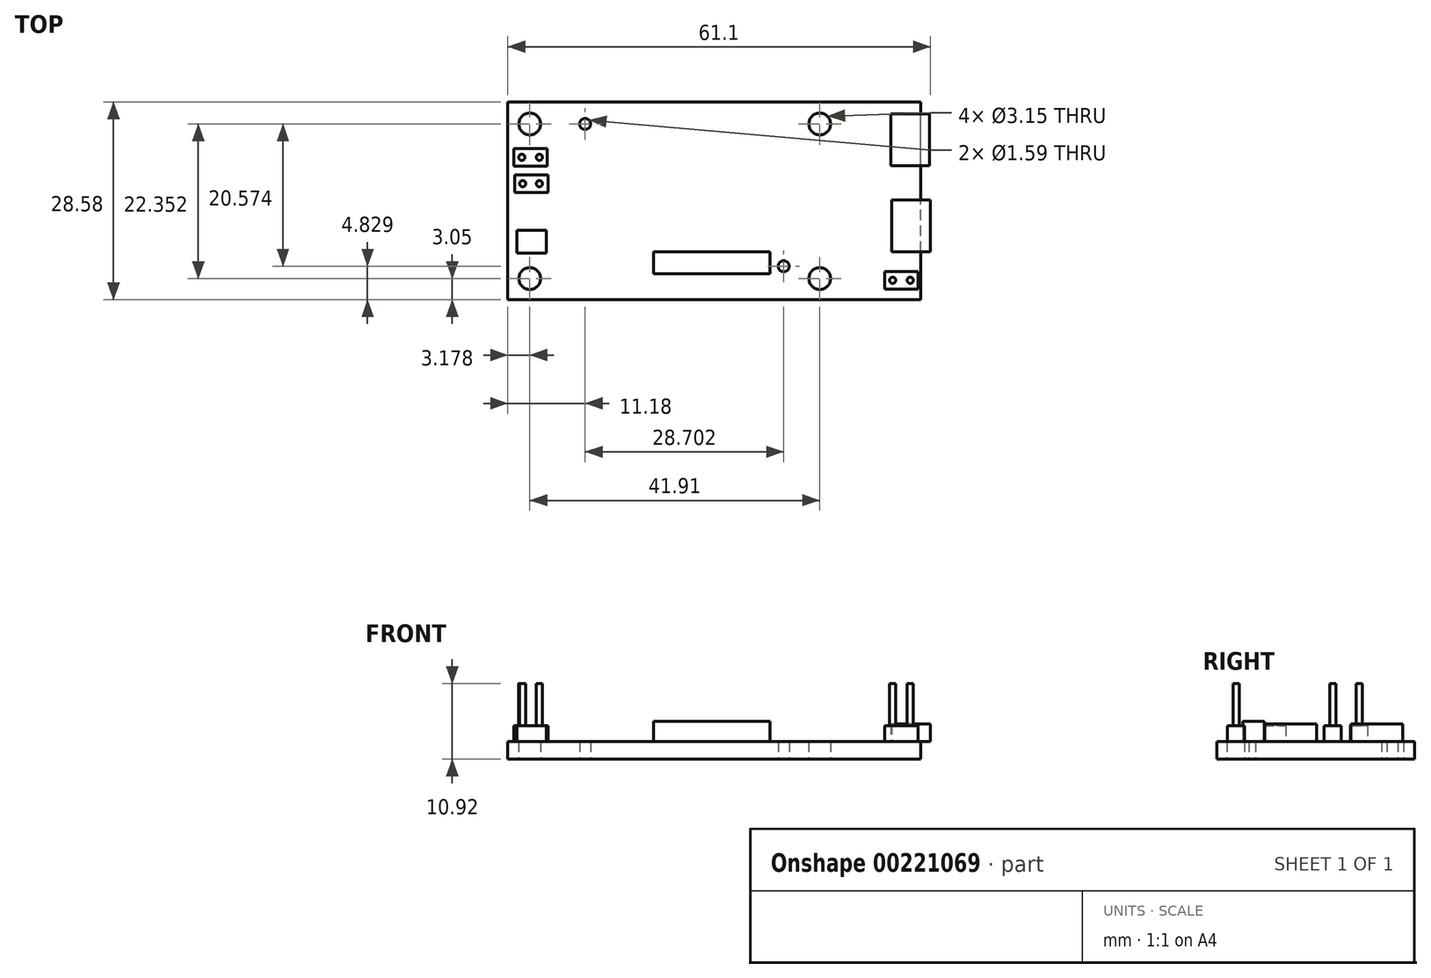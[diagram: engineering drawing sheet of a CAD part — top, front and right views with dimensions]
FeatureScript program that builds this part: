
annotation { "Feature Type Name" : "Feature", "Feature Type Description" : "" }
export const myFeature = defineFeature(function(context is Context, id is Id, definition is map)
    precondition{}
    {
        {
            var Q0;
            Q0=qCreatedBy(makeId("Top.planeOp"),FACE);
            var sketch = newSketch(context, id + "F0", { "sketchPlane" : qUnion([Q0])});
            skLineSegment(sketch, "E0", {"start": v(-22.44, -2) * mm, "end": v(-22.44, -0.67) * mm});
            skLineSegment(sketch, "E1", {"start": v(-22.44, -0.67) * mm, "end": v(-21.12, -0.67) * mm});
            skLineSegment(sketch, "E2", {"start": v(-21.12, -0.67) * mm, "end": v(-21.12, -2) * mm});
            skLineSegment(sketch, "E3", {"start": v(-21.12, -2) * mm, "end": v(-22.44, -2) * mm});
            skLineSegment(sketch, "E4", {"start": v(-22.44, 0.55) * mm, "end": v(-22.44, 1.87) * mm});
            skLineSegment(sketch, "E5", {"start": v(-22.44, 1.87) * mm, "end": v(-21.12, 1.87) * mm});
            skLineSegment(sketch, "E6", {"start": v(-21.12, 1.87) * mm, "end": v(-21.12, 0.55) * mm});
            skLineSegment(sketch, "E7", {"start": v(-21.12, 0.55) * mm, "end": v(-22.44, 0.55) * mm});
            skLineSegment(sketch, "E8", {"start": v(-22.44, 3.09) * mm, "end": v(-22.44, 4.4) * mm});
            skLineSegment(sketch, "E9", {"start": v(-22.44, 4.4) * mm, "end": v(-21.12, 4.4) * mm});
            skLineSegment(sketch, "E10", {"start": v(-21.12, 4.4) * mm, "end": v(-21.12, 3.09) * mm});
            skLineSegment(sketch, "E11", {"start": v(-21.12, 3.09) * mm, "end": v(-22.44, 3.09) * mm});
            skLineSegment(sketch, "E12", {"start": v(-22.44, 5.63) * mm, "end": v(-22.44, 6.95) * mm});
            skLineSegment(sketch, "E13", {"start": v(-22.44, 6.95) * mm, "end": v(-21.12, 6.95) * mm});
            skLineSegment(sketch, "E14", {"start": v(-21.12, 6.95) * mm, "end": v(-21.12, 5.63) * mm});
            skLineSegment(sketch, "E15", {"start": v(-21.12, 5.63) * mm, "end": v(-22.44, 5.63) * mm});
            skLineSegment(sketch, "E16", {"start": v(26.9, -10.78) * mm, "end": v(28.33, -10.78) * mm});
            skLineSegment(sketch, "E17", {"start": v(28.33, -10.78) * mm, "end": v(28.33, -12.2) * mm});
            skLineSegment(sketch, "E18", {"start": v(28.33, -12.2) * mm, "end": v(26.9, -12.2) * mm});
            skLineSegment(sketch, "E19", {"start": v(26.9, -12.2) * mm, "end": v(26.9, -10.78) * mm});
            skLineSegment(sketch, "E20", {"start": v(-27.68, 1.77) * mm, "end": v(-29.1, 1.77) * mm});
            skLineSegment(sketch, "E21", {"start": v(-29.1, 1.77) * mm, "end": v(-29.1, 3.19) * mm});
            skLineSegment(sketch, "E22", {"start": v(-29.1, 3.19) * mm, "end": v(-27.68, 3.19) * mm});
            skLineSegment(sketch, "E23", {"start": v(-27.68, 3.19) * mm, "end": v(-27.68, 1.77) * mm});
            skLineSegment(sketch, "E24", {"start": v(-27.8, 5.58) * mm, "end": v(-29.23, 5.58) * mm});
            skLineSegment(sketch, "E25", {"start": v(-29.23, 5.58) * mm, "end": v(-29.23, 7) * mm});
            skLineSegment(sketch, "E26", {"start": v(-29.23, 7) * mm, "end": v(-27.8, 7) * mm});
            skLineSegment(sketch, "E27", {"start": v(-27.8, 7) * mm, "end": v(-27.8, 5.58) * mm});
            skLineSegment(sketch, "E28", {"start": v(24.95, -7.37) * mm, "end": v(30.55, -7.37) * mm});
            skLineSegment(sketch, "E29", {"start": v(30.55, -7.37) * mm, "end": v(30.55, 0.13) * mm});
            skLineSegment(sketch, "E30", {"start": v(30.55, 0.13) * mm, "end": v(24.95, 0.13) * mm});
            skLineSegment(sketch, "E31", {"start": v(24.95, 0.13) * mm, "end": v(24.95, -7.37) * mm});
            skLineSegment(sketch, "E32", {"start": v(-29.24, -4.28) * mm, "end": v(-25, -4.28) * mm});
            skLineSegment(sketch, "E33", {"start": v(-25, -4.28) * mm, "end": v(-25, -7.53) * mm});
            skLineSegment(sketch, "E34", {"start": v(-25, -7.53) * mm, "end": v(-29.24, -7.53) * mm});
            skLineSegment(sketch, "E35", {"start": v(-29.24, -7.53) * mm, "end": v(-29.24, -4.28) * mm});
            skLineSegment(sketch, "E36", {"start": v(-23.05, -0.06) * mm, "end": v(-23.05, -2.6) * mm});
            skLineSegment(sketch, "E37", {"start": v(-23.05, -2.6) * mm, "end": v(2.35, -2.6) * mm});
            skLineSegment(sketch, "E38", {"start": v(2.35, -0.06) * mm, "end": v(-23.05, -0.06) * mm});
            skLineSegment(sketch, "E39", {"start": v(-23.05, 2.48) * mm, "end": v(-23.05, -0.06) * mm});
            skLineSegment(sketch, "E40", {"start": v(-23.05, -0.06) * mm, "end": v(2.35, -0.06) * mm});
            skLineSegment(sketch, "E41", {"start": v(2.35, 2.48) * mm, "end": v(-23.05, 2.48) * mm});
            skLineSegment(sketch, "E42", {"start": v(-23.05, 5.02) * mm, "end": v(-23.05, 2.48) * mm});
            skLineSegment(sketch, "E43", {"start": v(-23.05, 2.48) * mm, "end": v(2.35, 2.48) * mm});
            skLineSegment(sketch, "E44", {"start": v(2.35, 5.02) * mm, "end": v(-23.05, 5.02) * mm});
            skLineSegment(sketch, "E45", {"start": v(-23.05, 7.56) * mm, "end": v(-23.05, 5.02) * mm});
            skLineSegment(sketch, "E46", {"start": v(-23.05, 5.02) * mm, "end": v(2.35, 5.02) * mm});
            skLineSegment(sketch, "E47", {"start": v(2.35, 7.56) * mm, "end": v(-23.05, 7.56) * mm});
            skLineSegment(sketch, "E48", {"start": v(-9.46, -7.4) * mm, "end": v(7.34, -7.4) * mm});
            skLineSegment(sketch, "E49", {"start": v(7.34, -7.4) * mm, "end": v(7.34, -10.53) * mm});
            skLineSegment(sketch, "E50", {"start": v(7.34, -10.53) * mm, "end": v(-9.46, -10.53) * mm});
            skLineSegment(sketch, "E51", {"start": v(-9.46, -10.53) * mm, "end": v(-9.46, -7.4) * mm});
            skLineSegment(sketch, "E52", {"start": v(24.82, 5.08) * mm, "end": v(30.42, 5.08) * mm});
            skLineSegment(sketch, "E53", {"start": v(30.42, 5.08) * mm, "end": v(30.42, 12.58) * mm});
            skLineSegment(sketch, "E54", {"start": v(30.42, 12.58) * mm, "end": v(24.82, 12.58) * mm});
            skLineSegment(sketch, "E55", {"start": v(24.82, 12.58) * mm, "end": v(24.82, 5.08) * mm});
            skLineSegment(sketch, "E56", {"start": v(28.76, -10.25) * mm, "end": v(28.76, -12.74) * mm});
            skLineSegment(sketch, "E57", {"start": v(28.76, -12.74) * mm, "end": v(23.94, -12.74) * mm});
            skLineSegment(sketch, "E58", {"start": v(23.94, -12.74) * mm, "end": v(23.94, -10.25) * mm});
            skLineSegment(sketch, "E59", {"start": v(23.94, -10.25) * mm, "end": v(28.76, -10.25) * mm});
            skLineSegment(sketch, "E60", {"start": v(-29.53, 1.23) * mm, "end": v(-29.53, 3.72) * mm});
            skLineSegment(sketch, "E61", {"start": v(-29.53, 3.72) * mm, "end": v(-24.7, 3.72) * mm});
            skLineSegment(sketch, "E62", {"start": v(-24.7, 3.72) * mm, "end": v(-24.7, 1.23) * mm});
            skLineSegment(sketch, "E63", {"start": v(-24.7, 1.23) * mm, "end": v(-29.53, 1.23) * mm});
            skLineSegment(sketch, "E64", {"start": v(-29.66, 5.04) * mm, "end": v(-29.66, 7.53) * mm});
            skLineSegment(sketch, "E65", {"start": v(-29.66, 7.53) * mm, "end": v(-24.83, 7.53) * mm});
            skLineSegment(sketch, "E66", {"start": v(-24.83, 7.53) * mm, "end": v(-24.83, 5.04) * mm});
            skLineSegment(sketch, "E67", {"start": v(-24.83, 5.04) * mm, "end": v(-29.66, 5.04) * mm});
            skLineSegment(sketch, "E68", {"start": v(12.25, 5.02) * mm, "end": v(-13.15, 5.02) * mm});
            skLineSegment(sketch, "E69", {"start": v(-13.15, 5.02) * mm, "end": v(12.25, 5.02) * mm});
            skLineSegment(sketch, "E70", {"start": v(12.25, 5.02) * mm, "end": v(12.25, 7.56) * mm});
            skLineSegment(sketch, "E71", {"start": v(12.25, 7.56) * mm, "end": v(-13.15, 7.56) * mm});
            skLineSegment(sketch, "E72", {"start": v(12.25, -0.06) * mm, "end": v(-13.15, -0.06) * mm});
            skLineSegment(sketch, "E73", {"start": v(-13.15, -0.06) * mm, "end": v(12.25, -0.06) * mm});
            skLineSegment(sketch, "E74", {"start": v(12.25, -0.06) * mm, "end": v(12.25, 2.48) * mm});
            skLineSegment(sketch, "E75", {"start": v(12.25, 2.48) * mm, "end": v(-13.15, 2.48) * mm});
            skLineSegment(sketch, "E76", {"start": v(-13.15, 2.48) * mm, "end": v(12.25, 2.48) * mm});
            skLineSegment(sketch, "E77", {"start": v(12.25, 2.48) * mm, "end": v(12.25, 5.02) * mm});
            skLineSegment(sketch, "E78", {"start": v(-13.15, -2.6) * mm, "end": v(12.25, -2.6) * mm});
            skLineSegment(sketch, "E79", {"start": v(12.25, -2.6) * mm, "end": v(12.25, -0.06) * mm});
            skLineSegment(sketch, "E80", {"start": v(-30.55, 14.29) * mm, "end": v(-30.55, -14.29) * mm});
            skLineSegment(sketch, "E81", {"start": v(-30.55, -14.29) * mm, "end": v(29.14, -14.29) * mm});
            skLineSegment(sketch, "E82", {"start": v(29.14, -14.29) * mm, "end": v(29.14, 14.29) * mm});
            skLineSegment(sketch, "E83", {"start": v(29.14, 14.29) * mm, "end": v(-30.55, 14.29) * mm});
            skSolve(sketch);
        }
        {
            var Q0;
            Q0=qCreatedBy(makeId("Top.planeOp"),FACE);
            var sketch = newSketch(context, id + "F1", { "sketchPlane" : qUnion([Q0])});
            skLineSegment(sketch, "E84.0", {"start": v(-30.55, 14.29) * mm, "end": v(-30.55, -14.29) * mm});
            skLineSegment(sketch, "E84.1", {"start": v(-30.55, -14.29) * mm, "end": v(29.14, -14.29) * mm});
            skLineSegment(sketch, "E84.2", {"start": v(29.14, 14.29) * mm, "end": v(-30.55, 14.29) * mm});
            skLineSegment(sketch, "E84.3", {"start": v(29.14, -14.29) * mm, "end": v(29.14, 14.29) * mm});
            skCircle(sketch, "E85", {"center": v(-27.37, 11.11) * mm, "radius": 1.57 * mm});
            skCircle(sketch, "E86", {"center": v(14.54, 11.11) * mm, "radius": 1.57 * mm});
            skCircle(sketch, "E87", {"center": v(14.54, -11.24) * mm, "radius": 1.57 * mm});
            skCircle(sketch, "E88", {"center": v(-27.37, -11.24) * mm, "radius": 1.57 * mm});
            skCircle(sketch, "E89", {"center": v(-19.37, 11.11) * mm, "radius": 0.8 * mm});
            skCircle(sketch, "E90", {"center": v(9.33, -9.46) * mm, "radius": 0.8 * mm});
            skSolve(sketch);
        }
        {
            var Q0;
            Q0=qSketchRegion(id+"F1",true);
            extrude(context, id + "F2", {"entities" : qUnion([Q0]), "depth" : 2.54 * mm});
        }
        {
            var Q0;
            Q0=makeQuery(id+"F2.opExtrude","CAP_FACE",FACE,{"disambiguationData":[OSD([sQuery(id+"F1.wireOp",EDGE,"E84.0"),sQuery(id+"F1.wireOp",EDGE,"E84.1"),sQuery(id+"F1.wireOp",EDGE,"E84.2"),sQuery(id+"F1.wireOp",EDGE,"E84.3"),sQuery(id+"F1.wireOp",EDGE,"E85"),sQuery(id+"F1.wireOp",EDGE,"E86"),sQuery(id+"F1.wireOp",EDGE,"E87"),sQuery(id+"F1.wireOp",EDGE,"E88"),sQuery(id+"F1.wireOp",EDGE,"E89"),sQuery(id+"F1.wireOp",EDGE,"E90")])],"isStart":false});
            var sketch = newSketch(context, id + "F3", { "sketchPlane" : qUnion([Q0])});
            skLineSegment(sketch, "E91.0", {"start": v(30.42, 12.58) * mm, "end": v(24.82, 12.58) * mm});
            skLineSegment(sketch, "E91.1", {"start": v(30.42, 5.08) * mm, "end": v(30.42, 12.58) * mm});
            skLineSegment(sketch, "E91.2", {"start": v(24.82, 5.08) * mm, "end": v(30.42, 5.08) * mm});
            skLineSegment(sketch, "E91.3", {"start": v(24.82, 12.58) * mm, "end": v(24.82, 5.08) * mm});
            skLineSegment(sketch, "E91.4", {"start": v(30.55, 0.13) * mm, "end": v(24.95, 0.13) * mm});
            skLineSegment(sketch, "E91.5", {"start": v(30.55, -7.37) * mm, "end": v(30.55, 0.13) * mm});
            skLineSegment(sketch, "E91.6", {"start": v(24.95, -7.37) * mm, "end": v(30.55, -7.37) * mm});
            skLineSegment(sketch, "E91.7", {"start": v(24.95, 0.13) * mm, "end": v(24.95, -7.37) * mm});
            skSolve(sketch);
        }
        {
            var Q0;
            Q0=qSketchRegion(id+"F3",true);
            extrude(context, id + "F4", {"entities" : qUnion([Q0]), "operationType" : NewBodyOperationType.ADD, "depth" : 2.54 * mm});
        }
        {
            var Q0;
            Q0=makeQuery(id+"F2.opExtrude","CAP_FACE",FACE,{"disambiguationData":[OSD([sQuery(id+"F1.wireOp",EDGE,"E84.0"),sQuery(id+"F1.wireOp",EDGE,"E84.1"),sQuery(id+"F1.wireOp",EDGE,"E84.2"),sQuery(id+"F1.wireOp",EDGE,"E84.3"),sQuery(id+"F1.wireOp",EDGE,"E85"),sQuery(id+"F1.wireOp",EDGE,"E86"),sQuery(id+"F1.wireOp",EDGE,"E87"),sQuery(id+"F1.wireOp",EDGE,"E88"),sQuery(id+"F1.wireOp",EDGE,"E89"),sQuery(id+"F1.wireOp",EDGE,"E90")])],"isStart":false});
            var sketch = newSketch(context, id + "F5", { "sketchPlane" : qUnion([Q0])});
            skLineSegment(sketch, "E92.0", {"start": v(-9.46, -7.4) * mm, "end": v(7.34, -7.4) * mm});
            skLineSegment(sketch, "E92.1", {"start": v(7.34, -7.4) * mm, "end": v(7.34, -10.53) * mm});
            skLineSegment(sketch, "E92.2", {"start": v(7.34, -10.53) * mm, "end": v(-9.46, -10.53) * mm});
            skLineSegment(sketch, "E92.3", {"start": v(-9.46, -10.53) * mm, "end": v(-9.46, -7.4) * mm});
            skSolve(sketch);
        }
        {
            var Q0;
            Q0=qSketchRegion(id+"F5",true);
            extrude(context, id + "F6", {"entities" : qUnion([Q0]), "operationType" : NewBodyOperationType.ADD, "depth" : 2.92 * mm});
        }
        {
            var Q0;
            Q0=makeQuery(id+"F2.opExtrude","CAP_FACE",FACE,{"disambiguationData":[OSD([sQuery(id+"F1.wireOp",EDGE,"E84.0"),sQuery(id+"F1.wireOp",EDGE,"E84.1"),sQuery(id+"F1.wireOp",EDGE,"E84.2"),sQuery(id+"F1.wireOp",EDGE,"E84.3"),sQuery(id+"F1.wireOp",EDGE,"E85"),sQuery(id+"F1.wireOp",EDGE,"E86"),sQuery(id+"F1.wireOp",EDGE,"E87"),sQuery(id+"F1.wireOp",EDGE,"E88"),sQuery(id+"F1.wireOp",EDGE,"E89"),sQuery(id+"F1.wireOp",EDGE,"E90")])],"isStart":false});
            var sketch = newSketch(context, id + "F7", { "sketchPlane" : qUnion([Q0])});
            skLineSegment(sketch, "E93.0", {"start": v(23.94, -10.25) * mm, "end": v(28.76, -10.25) * mm});
            skLineSegment(sketch, "E93.1", {"start": v(23.94, -12.74) * mm, "end": v(23.94, -10.25) * mm});
            skLineSegment(sketch, "E93.2", {"start": v(28.76, -12.74) * mm, "end": v(23.94, -12.74) * mm});
            skLineSegment(sketch, "E93.3", {"start": v(28.76, -10.25) * mm, "end": v(28.76, -12.74) * mm});
            skLineSegment(sketch, "E93.4", {"start": v(-24.83, 5.04) * mm, "end": v(-29.66, 5.04) * mm});
            skLineSegment(sketch, "E93.5", {"start": v(-24.83, 7.53) * mm, "end": v(-24.83, 5.04) * mm});
            skLineSegment(sketch, "E93.6", {"start": v(-29.66, 7.53) * mm, "end": v(-24.83, 7.53) * mm});
            skLineSegment(sketch, "E93.7", {"start": v(-29.66, 5.04) * mm, "end": v(-29.66, 7.53) * mm});
            skLineSegment(sketch, "E93.8", {"start": v(-29.53, 1.23) * mm, "end": v(-29.53, 3.72) * mm});
            skLineSegment(sketch, "E93.9", {"start": v(-29.53, 3.72) * mm, "end": v(-24.7, 3.72) * mm});
            skLineSegment(sketch, "E93.10", {"start": v(-24.7, 3.72) * mm, "end": v(-24.7, 1.23) * mm});
            skLineSegment(sketch, "E93.11", {"start": v(-24.7, 1.23) * mm, "end": v(-29.53, 1.23) * mm});
            skLineSegment(sketch, "E93.12", {"start": v(-29.24, -4.28) * mm, "end": v(-25, -4.28) * mm});
            skLineSegment(sketch, "E93.13", {"start": v(-25, -4.28) * mm, "end": v(-25, -7.53) * mm});
            skLineSegment(sketch, "E93.14", {"start": v(-25, -7.53) * mm, "end": v(-29.24, -7.53) * mm});
            skLineSegment(sketch, "E93.15", {"start": v(-29.24, -7.53) * mm, "end": v(-29.24, -4.28) * mm});
            skSolve(sketch);
        }
        {
            var Q0;
            Q0=qSketchRegion(id+"F7",true);
            extrude(context, id + "F8", {"entities" : qUnion([Q0]), "operationType" : NewBodyOperationType.ADD, "depth" : 2.3 * mm});
        }
        {
            var Q0;
            Q0=makeQuery(id+"F8.opExtrude","CAP_FACE",FACE,{"disambiguationData":[OSD([sQuery(id+"F7.wireOp",EDGE,"E93.4"),sQuery(id+"F7.wireOp",EDGE,"E93.5"),sQuery(id+"F7.wireOp",EDGE,"E93.6"),sQuery(id+"F7.wireOp",EDGE,"E93.7")])],"isStart":false});
            var sketch = newSketch(context, id + "F9", { "sketchPlane" : qUnion([Q0])});
            skCircle(sketch, "E94", {"center": v(-28.51, 6.29) * mm, "radius": 0.44 * mm});
            skCircle(sketch, "E95", {"center": v(-25.97, 6.29) * mm, "radius": 0.44 * mm});
            skCircle(sketch, "E96", {"center": v(-28.39, 2.48) * mm, "radius": 0.44 * mm});
            skCircle(sketch, "E97", {"center": v(-25.97, 2.48) * mm, "radius": 0.44 * mm});
            skCircle(sketch, "E98", {"center": v(27.62, -11.5) * mm, "radius": 0.44 * mm});
            skCircle(sketch, "E99", {"center": v(25.08, -11.5) * mm, "radius": 0.44 * mm});
            skPoint(sketch, "E100.0", {"position": v(28.33, -10.78) * mm});
            skPoint(sketch, "E100.1", {"position": v(26.9, -12.2) * mm});
            skLineSegment(sketch, "E101", {"start": v(28.33, -10.78) * mm, "end": v(26.9, -12.2) * mm, "construction": true});
            skPoint(sketch, "E102.0", {"position": v(-27.8, 7) * mm});
            skPoint(sketch, "E102.1", {"position": v(-29.23, 5.58) * mm});
            skPoint(sketch, "E102.2", {"position": v(-29.1, 3.19) * mm});
            skPoint(sketch, "E102.3", {"position": v(-27.68, 1.77) * mm});
            skLineSegment(sketch, "E103", {"start": v(-27.8, 7) * mm, "end": v(-29.23, 5.58) * mm, "construction": true});
            skLineSegment(sketch, "E104", {"start": v(-29.1, 3.19) * mm, "end": v(-27.68, 1.77) * mm, "construction": true});
            skSolve(sketch);
        }
        {
            var Q0;
            Q0=qSketchRegion(id+"F9",true);
            extrude(context, id + "F10", {"entities" : qUnion([Q0]), "operationType" : NewBodyOperationType.ADD, "depth" : 6.1 * mm});
        }
    });
